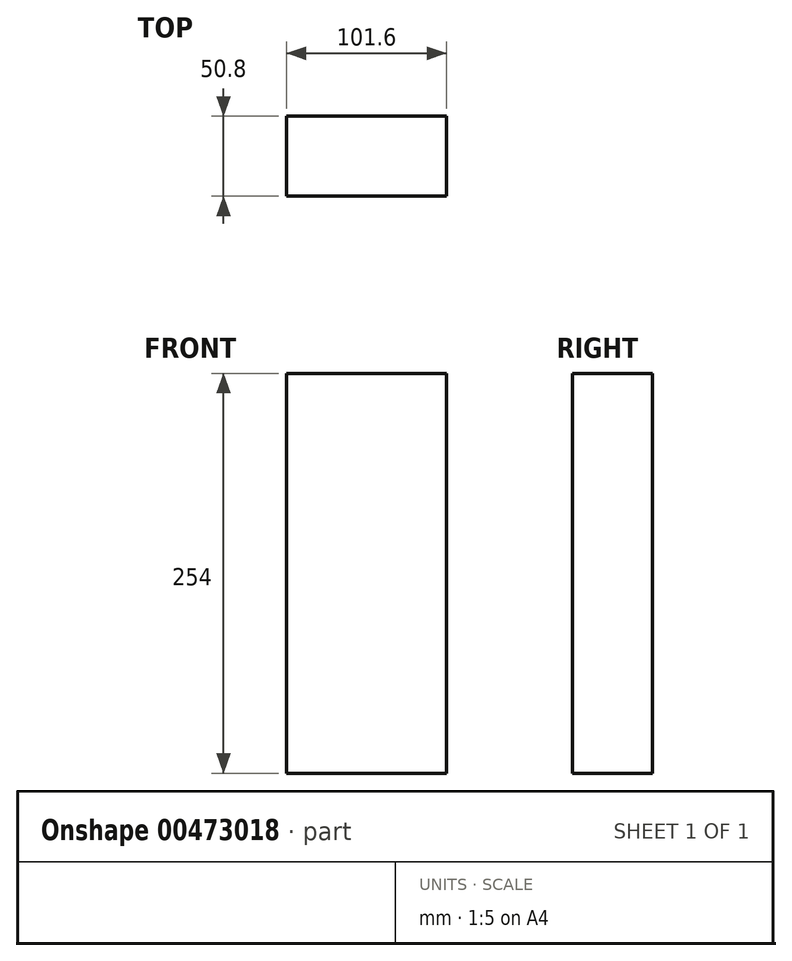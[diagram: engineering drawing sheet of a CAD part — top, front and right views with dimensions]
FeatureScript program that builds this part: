
annotation { "Feature Type Name" : "Feature", "Feature Type Description" : "" }
export const myFeature = defineFeature(function(context is Context, id is Id, definition is map)
    precondition{}
    {
        {
            var Q0;
            Q0=qCreatedBy(makeId("Top.planeOp"),FACE);
            var sketch = newSketch(context, id + "F0", { "sketchPlane" : qUnion([Q0])});
            skLineSegment(sketch, "E0.bottom", {"start": v(50.8, 25.4) * mm, "end": v(-50.8, 25.4) * mm});
            skLineSegment(sketch, "E0.top", {"start": v(50.8, -25.4) * mm, "end": v(-50.8, -25.4) * mm});
            skLineSegment(sketch, "E0.left", {"start": v(50.8, 25.4) * mm, "end": v(50.8, -25.4) * mm});
            skLineSegment(sketch, "E0.right", {"start": v(-50.8, 25.4) * mm, "end": v(-50.8, -25.4) * mm});
            skPoint(sketch, "E0.middle", {"position": v(0, 0) * mm});
            skSolve(sketch);
        }
        {
            var Q0;
            Q0 = qSketchRegion(id + "F0", true);
            extrude(context, id + "F1", {"entities" : qUnion([Q0]), "depth" : 254 * mm, "offsetDistance" : 25.4 * mm});
        }
    });
